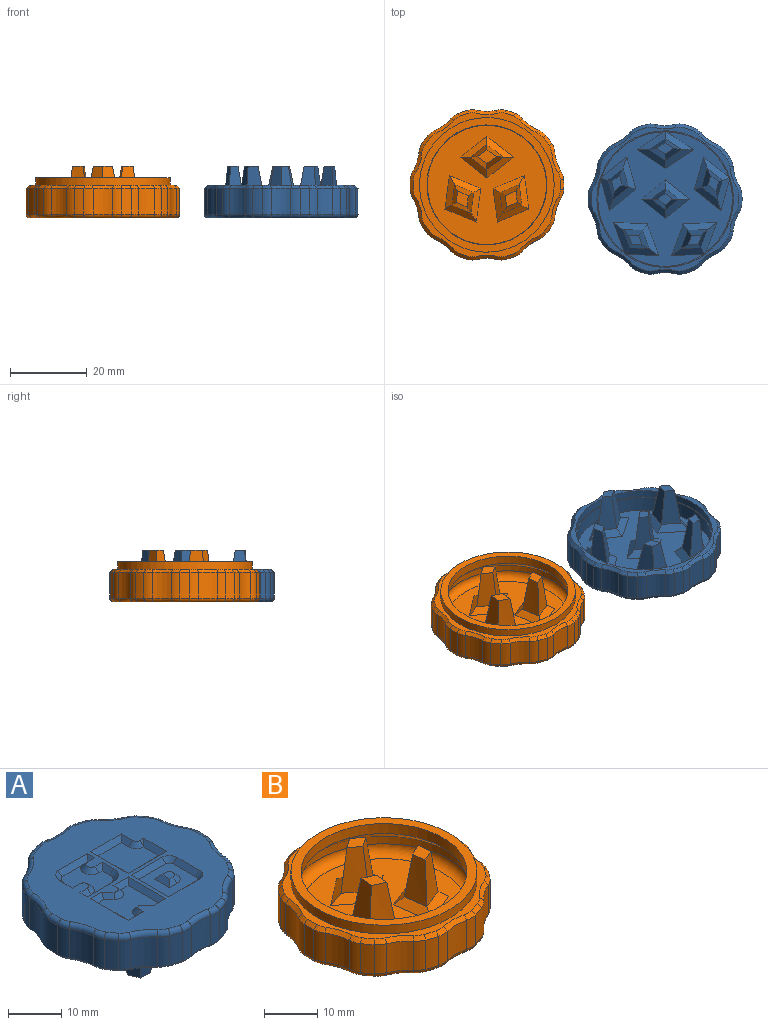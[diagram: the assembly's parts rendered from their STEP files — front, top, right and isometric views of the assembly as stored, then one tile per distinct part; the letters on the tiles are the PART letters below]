
ASSEMBLY  parts=2 mates=1
PART A: 228 faces, bbox 40.8x39.9x13.5 mm
  f0: plane 38x37.08mm, normal (0,0,1), area 717.1mm2, adj f59,f60,f61,f62,f63,f64,f65,f66
  f1: cylinder r=17.5mm len=35mm, axis (0,0,1), area 439.6mm2, adj f2,f33,f35,f37,f39,f45,f47,f49
  f2: plane 35x35mm, normal (0,0,-1), area 545.3mm2, adj f1,f33,f34,f35,f36,f37,f38,f39
  f3: plane 3.55x2.58mm, normal (0,0,-1), area 6.3mm2, adj f4,f5,f6,f7
  f4: bspline ~9.52x5.14mm, area 36.8mm2, adj f3,f5,f7,f53,f55
  f5: bspline ~11x5.19mm, area 36.8mm2, adj f3,f4,f6,f54,f56
  f6: bspline ~11x5.4mm, area 36mm2, adj f3,f5,f7,f56
  f7: bspline ~11x5.07mm, area 36mm2, adj f3,f4,f6,f55
  f8: plane 3.55x2.58mm, normal (0,0,-1), area 6.3mm2, adj f9,f10,f11,f12
  f9: bspline ~11x5.19mm, area 36.8mm2, adj f8,f10,f12,f49,f50
  f10: bspline ~9.52x5.14mm, area 36.8mm2, adj f8,f9,f11,f51,f52
  f11: bspline ~11x5.07mm, area 36mm2, adj f8,f10,f12,f51
  f12: bspline ~11x5.4mm, area 36mm2, adj f8,f9,f11,f49
  f13: plane 4.17x2.73mm, normal (0,0,-1), area 6.3mm2, adj f14,f15,f16,f17
  f14: bspline ~11x4.34mm, area 36.8mm2, adj f13,f15,f17,f45,f46
  f15: bspline ~9.52x4.95mm, area 36.8mm2, adj f13,f14,f16,f47,f48
  f16: bspline ~11x4.24mm, area 36mm2, adj f13,f15,f17,f47
  f17: bspline ~11x5.21mm, area 36mm2, adj f13,f14,f16,f45
  f18: plane 3.8x3.04mm, normal (0,0,-1), area 5.8mm2, adj f19,f20,f21,f22
  f19: plane 9.44x3.49mm, normal (0.62,0.78,-0.1), area 32.7mm2, adj f18,f20,f22,f41
  f20: plane 9.44x3.49mm, normal (0.62,-0.78,-0.1), area 32.7mm2, adj f18,f19,f21,f42
  f21: plane 9.44x3.49mm, normal (-0.62,-0.78,-0.1), area 32.7mm2, adj f18,f20,f22,f44
  f22: plane 9.44x3.49mm, normal (-0.62,0.78,-0.1), area 32.7mm2, adj f18,f19,f21,f43
  f23: plane 4.17x2.73mm, normal (0,0,-1), area 6.3mm2, adj f24,f25,f26,f27
  f24: bspline ~11x5.32mm, area 36.8mm2, adj f23,f25,f27,f33,f34
  f25: bspline ~11x4.34mm, area 36.8mm2, adj f23,f24,f26,f35,f36
  f26: bspline ~11x5.21mm, area 36mm2, adj f23,f25,f27,f35
  f27: bspline ~11x4.24mm, area 36mm2, adj f23,f24,f26,f33
  f28: plane 4.39x2.87mm, normal (0,0,-1), area 6.3mm2, adj f29,f30,f31,f32
  f29: bspline ~11x4.5mm, area 36mm2, adj f28,f30,f32,f37
  f30: bspline ~9.52x4.28mm, area 36.8mm2, adj f28,f29,f31,f37,f38
  f31: bspline ~11x4.6mm, area 36.8mm2, adj f28,f30,f32,f39,f40
  f32: bspline ~11x4.5mm, area 36mm2, adj f28,f29,f31,f39
  f33: bspline ~8.64x7.34mm, area 16mm2, adj f1,f2,f24,f27,f34,f35
  f34: bspline ~8.91x4.02mm, area 15.8mm2, adj f2,f24,f33,f36
  f35: bspline ~9.75x4.27mm, area 16mm2, adj f1,f2,f25,f26,f33,f36
  f36: bspline ~7.94x6.79mm, area 15.8mm2, adj f2,f25,f34,f35
  f37: bspline ~8.99x6.79mm, area 16mm2, adj f1,f2,f29,f30,f38,f39
  f38: bspline ~8.25x6.29mm, area 15.8mm2, adj f2,f30,f37,f40
  f39: bspline ~8.99x6.79mm, area 16mm2, adj f1,f2,f31,f32,f37,f40
  f40: bspline ~8.25x6.29mm, area 15.8mm2, adj f2,f31,f38,f39
  f41: plane 6.26x5.01mm, normal (0.42,0.52,-0.74), area 14.5mm2, adj f2,f19,f42,f43
  f42: plane 6.26x5.01mm, normal (0.42,-0.52,-0.74), area 14.5mm2, adj f2,f20,f41,f44
  f43: plane 6.26x5.01mm, normal (-0.42,0.52,-0.74), area 14.5mm2, adj f2,f22,f41,f44
  f44: plane 6.26x5.01mm, normal (-0.42,-0.52,-0.74), area 14.5mm2, adj f2,f21,f42,f43
  f45: bspline ~9.75x4.27mm, area 16mm2, adj f1,f2,f14,f17,f46,f47
  f46: bspline ~7.94x6.79mm, area 15.8mm2, adj f2,f14,f45,f48
  f47: bspline ~8.64x7.34mm, area 16mm2, adj f1,f2,f15,f16,f45,f48
  f48: bspline ~8.91x4.02mm, area 15.8mm2, adj f2,f15,f46,f47
  f49: bspline ~8.71x2.09mm, area 16mm2, adj f1,f2,f9,f12,f50,f51
  f50: bspline ~8.82x4.66mm, area 15.8mm2, adj f2,f9,f49,f52
  f51: bspline ~9.64x4.98mm, area 16mm2, adj f1,f2,f10,f11,f49,f52
  f52: bspline ~9.71x2.11mm, area 15.8mm2, adj f2,f10,f50,f51
  f53: bspline ~9.71x2.11mm, area 15.8mm2, adj f2,f4,f54,f55
  f54: bspline ~8.82x4.66mm, area 15.8mm2, adj f2,f5,f53,f56
  f55: bspline ~9.64x4.98mm, area 16mm2, adj f1,f2,f4,f7,f53,f56
  f56: bspline ~8.71x2.09mm, area 16mm2, adj f1,f2,f5,f6,f54,f55
  f57: cylinder r=17.75mm len=35.5mm, axis (0,0,-1), area 223.1mm2, adj f58,f139
  f58: plane 35.5x35.5mm, normal (0,0,-1), area 27.7mm2, adj f1,f57
  f59: torus R=4mm, axis (0,0,1), area 3.5mm2, adj f0,f60,f98,f99
  f60: torus R=11.9mm, axis (0,0,1), area 8.3mm2, adj f0,f59,f61,f100
  f61: torus R=4mm, axis (0,0,1), area 3.5mm2, adj f0,f60,f62,f101
  f62: torus R=19mm, axis (0,0,1), area 4mm2, adj f0,f61,f63,f102
  f63: torus R=4mm, axis (0,0,1), area 3.5mm2, adj f0,f62,f64,f103
  f64: torus R=11.9mm, axis (0,0,1), area 8.3mm2, adj f0,f63,f65,f104
  f65: torus R=4mm, axis (0,0,1), area 3.5mm2, adj f0,f64,f66,f105
  f66: torus R=19mm, axis (0,0,1), area 4mm2, adj f0,f65,f67,f106
  f67: torus R=4mm, axis (0,0,1), area 3.5mm2, adj f0,f66,f68,f107
  f68: torus R=11.9mm, axis (0,0,1), area 8.3mm2, adj f0,f67,f69,f108
  f69: torus R=4mm, axis (0,0,1), area 3.5mm2, adj f0,f68,f70,f109
  f70: torus R=19mm, axis (0,0,1), area 4mm2, adj f0,f69,f71,f110
  f71: torus R=4mm, axis (0,0,1), area 3.5mm2, adj f0,f70,f72,f111
  f72: torus R=11.9mm, axis (0,0,1), area 8.3mm2, adj f0,f71,f73,f112
  f73: torus R=4mm, axis (0,0,1), area 3.5mm2, adj f0,f72,f74,f113
  f74: torus R=19mm, axis (0,0,1), area 4mm2, adj f0,f73,f75,f114
  f75: torus R=4mm, axis (0,0,1), area 3.5mm2, adj f0,f74,f76,f115
  f76: torus R=11.9mm, axis (0,0,1), area 8.3mm2, adj f0,f75,f77,f116
  f77: torus R=4mm, axis (0,0,1), area 3.5mm2, adj f0,f76,f78,f117
  f78: torus R=19mm, axis (0,0,1), area 4mm2, adj f0,f77,f79,f118
  f79: torus R=4mm, axis (0,0,1), area 3.5mm2, adj f0,f78,f80,f119
  f80: torus R=11.9mm, axis (0,0,1), area 8.3mm2, adj f0,f79,f81,f120
  f81: torus R=4mm, axis (0,0,1), area 3.5mm2, adj f0,f80,f82,f121
  f82: torus R=19mm, axis (0,0,1), area 4mm2, adj f0,f81,f83,f122
  f83: torus R=4mm, axis (0,0,1), area 3.5mm2, adj f0,f82,f84,f123
  f84: torus R=11.9mm, axis (0,0,1), area 8.3mm2, adj f0,f83,f85,f124
  f85: torus R=4mm, axis (0,0,1), area 3.5mm2, adj f0,f84,f86,f125
  f86: torus R=19mm, axis (0,0,1), area 4mm2, adj f0,f85,f87,f126
  f87: torus R=4mm, axis (0,0,1), area 3.5mm2, adj f0,f86,f88,f127
  f88: torus R=11.9mm, axis (0,0,1), area 8.3mm2, adj f0,f87,f89,f128
  f89: torus R=4mm, axis (0,0,1), area 3.5mm2, adj f0,f88,f90,f129
  f90: torus R=19mm, axis (0,0,1), area 4mm2, adj f0,f89,f91,f130
  f91: torus R=4mm, axis (0,0,1), area 3.5mm2, adj f0,f90,f92,f131
  f92: torus R=11.9mm, axis (0,0,1), area 8.3mm2, adj f0,f91,f93,f132
  f93: torus R=4mm, axis (0,0,1), area 3.5mm2, adj f0,f92,f94,f133
  f94: torus R=19mm, axis (0,0,1), area 4mm2, adj f0,f93,f95,f134
  f95: torus R=4mm, axis (0,0,1), area 3.5mm2, adj f0,f94,f96,f135
  f96: torus R=11.9mm, axis (0,0,1), area 8.3mm2, adj f0,f95,f97,f136
  f97: torus R=4mm, axis (0,0,1), area 3.5mm2, adj f0,f96,f98,f137
  f98: torus R=19mm, axis (0,0,1), area 4mm2, adj f0,f59,f97,f138
  f99: cylinder r=5mm len=6.7mm, axis (0,0,1), area 16.2mm2, adj f59,f100,f138,f208
  f100: cylinder r=10.9mm len=6.7mm, axis (0,0,-1), area 34.2mm2, adj f60,f99,f101,f210
  f101: cylinder r=5mm len=6.7mm, axis (0,0,1), area 16.2mm2, adj f61,f100,f102,f212
  f102: cylinder r=20mm len=6.7mm, axis (0,0,-1), area 17.6mm2, adj f62,f101,f103,f214
  f103: cylinder r=5mm len=6.7mm, axis (0,0,1), area 16.2mm2, adj f63,f102,f104,f216
  f104: cylinder r=10.9mm len=6.7mm, axis (0,0,-1), area 34.2mm2, adj f64,f103,f105,f218
  f105: cylinder r=5mm len=6.7mm, axis (0,0,1), area 16.2mm2, adj f65,f104,f106,f220
  f106: cylinder r=20mm len=6.7mm, axis (0,0,-1), area 17.6mm2, adj f66,f105,f107,f222
  f107: cylinder r=5mm len=6.7mm, axis (0,0,1), area 16.2mm2, adj f67,f106,f108,f224
  f108: cylinder r=10.9mm len=6.7mm, axis (0,0,-1), area 34.2mm2, adj f68,f107,f109,f226
  f109: cylinder r=5mm len=6.7mm, axis (0,0,1), area 16.2mm2, adj f69,f108,f110,f227
  f110: cylinder r=20mm len=6.7mm, axis (0,0,-1), area 17.6mm2, adj f70,f109,f111,f225
  f111: cylinder r=5mm len=6.7mm, axis (0,0,1), area 16.2mm2, adj f71,f110,f112,f223
  f112: cylinder r=10.9mm len=6.7mm, axis (0,0,-1), area 34.2mm2, adj f72,f111,f113,f221
  f113: cylinder r=5mm len=6.7mm, axis (0,0,1), area 16.2mm2, adj f73,f112,f114,f219
  f114: cylinder r=20mm len=6.7mm, axis (0,0,-1), area 17.6mm2, adj f74,f113,f115,f217
  f115: cylinder r=5mm len=6.7mm, axis (0,0,1), area 16.2mm2, adj f75,f114,f116,f215
  f116: cylinder r=10.9mm len=6.7mm, axis (0,0,-1), area 34.2mm2, adj f76,f115,f117,f213
  f117: cylinder r=5mm len=6.7mm, axis (0,0,1), area 16.2mm2, adj f77,f116,f118,f211
  f118: cylinder r=20mm len=6.7mm, axis (0,0,-1), area 17.6mm2, adj f78,f117,f119,f209
  f119: cylinder r=5mm len=6.7mm, axis (0,0,1), area 16.2mm2, adj f79,f118,f120,f207
  f120: cylinder r=10.9mm len=6.7mm, axis (0,0,-1), area 34.2mm2, adj f80,f119,f121,f205
  f121: cylinder r=5mm len=6.7mm, axis (0,0,1), area 16.2mm2, adj f81,f120,f122,f203
  f122: cylinder r=20mm len=6.7mm, axis (0,0,-1), area 17.6mm2, adj f82,f121,f123,f201
  f123: cylinder r=5mm len=6.7mm, axis (0,0,1), area 16.2mm2, adj f83,f122,f124,f199
  f124: cylinder r=10.9mm len=6.7mm, axis (0,0,-1), area 34.2mm2, adj f84,f123,f125,f197
  f125: cylinder r=5mm len=6.7mm, axis (0,0,1), area 16.2mm2, adj f85,f124,f126,f195
  f126: cylinder r=20mm len=6.7mm, axis (0,0,-1), area 17.6mm2, adj f86,f125,f127,f193
  f127: cylinder r=5mm len=6.7mm, axis (0,0,1), area 16.2mm2, adj f87,f126,f128,f191
  f128: cylinder r=10.9mm len=6.7mm, axis (0,0,-1), area 34.2mm2, adj f88,f127,f129,f189
  f129: cylinder r=5mm len=6.7mm, axis (0,0,1), area 16.2mm2, adj f89,f128,f130,f188
  f130: cylinder r=20mm len=6.7mm, axis (0,0,-1), area 17.6mm2, adj f90,f129,f131,f190
  f131: cylinder r=5mm len=6.7mm, axis (0,0,1), area 16.2mm2, adj f91,f130,f132,f192
  f132: cylinder r=10.9mm len=6.7mm, axis (0,0,-1), area 34.2mm2, adj f92,f131,f133,f194
  f133: cylinder r=5mm len=6.7mm, axis (0,0,1), area 16.2mm2, adj f93,f132,f134,f196
  f134: cylinder r=20mm len=6.7mm, axis (0,0,-1), area 17.6mm2, adj f94,f133,f135,f198
  f135: cylinder r=5mm len=6.7mm, axis (0,0,1), area 16.2mm2, adj f95,f134,f136,f200
  f136: cylinder r=10.9mm len=6.7mm, axis (0,0,-1), area 34.2mm2, adj f96,f135,f137,f202
  f137: cylinder r=5mm len=6.7mm, axis (0,0,1), area 16.2mm2, adj f97,f136,f138,f204
  f138: cylinder r=20mm len=6.7mm, axis (0,0,-1), area 17.6mm2, adj f98,f99,f137,f206
  f139: plane 38.4x37.48mm, normal (0,0,-1), area 123.8mm2, adj f57,f188,f189,f190,f191,f192,f193,f194
  f140: plane 3x1mm, normal (0,0.71,0.71), area 3.2mm2, adj f0,f141,f151,f152
  f141: plane 10x1mm, normal (-0.71,0,0.71), area 12.7mm2, adj f0,f140,f142,f152
  f142: plane 4x1mm, normal (0,-0.71,0.71), area 4.2mm2, adj f0,f141,f143,f152
  f143: plane 1.07x1mm, normal (0.71,0,0.71), area 0.8mm2, adj f0,f142,f144,f152
  f144: cone r=0.8mm half-angle=45deg, axis (0,0,-1), area 4.3mm2, adj f0,f143,f145,f152
  f145: plane 2.34x2.05mm, normal (-0.5,-0.5,0.71), area 3mm2, adj f0,f144,f146,f152
  f146: plane 3x1mm, normal (0,-0.71,0.71), area 3.2mm2, adj f0,f145,f147,f152
  f147: plane 10x1mm, normal (0.71,0,0.71), area 12.7mm2, adj f0,f146,f148,f152
  f148: plane 4x1mm, normal (0,0.71,0.71), area 4.2mm2, adj f0,f147,f149,f152
  f149: plane 1.07x1mm, normal (-0.71,0,0.71), area 0.8mm2, adj f0,f148,f150,f152
  f150: cone r=0.8mm half-angle=45deg, axis (0,0,-1), area 4.3mm2, adj f0,f149,f151,f152
  f151: plane 2.34x2.05mm, normal (0.5,0.5,0.71), area 3mm2, adj f0,f140,f150,f152
  f152: plane 8x8mm, normal (0,0,1), area 52.5mm2, adj f140,f141,f142,f143,f144,f145,f146,f147
  f153: plane 10.2x1mm, normal (0,0.71,0.71), area 13mm2, adj f0,f154,f159,f160
  f154: plane 6x1mm, normal (-0.71,0,0.71), area 7.1mm2, adj f0,f153,f155,f160
  f155: plane 1x1mm, normal (0,-0.71,0.71), area 0.7mm2, adj f0,f154,f156
  f156: cone r=1mm half-angle=45deg, axis (0,0,-1), area 3.3mm2, adj f0,f155,f157,f160
  f157: plane 3x1mm, normal (-0.71,0,0.71), area 3.5mm2, adj f0,f156,f158,f160
  f158: plane 8.2x1mm, normal (0,-0.71,0.71), area 10.2mm2, adj f0,f157,f159,f160
  f159: plane 10x1mm, normal (0.71,0,0.71), area 12.7mm2, adj f0,f153,f158,f160
  f160: plane 8.2x8mm, normal (0,0,1), area 58.5mm2, adj f153,f154,f156,f157,f158,f159
  f161: cone r=3mm half-angle=45deg, axis (0,0,1), area 4.2mm2, adj f0,f162,f174,f175
  f162: plane 3.17x1mm, normal (0.71,0,0.71), area 3.8mm2, adj f0,f161,f163,f175
  f163: plane 2x1mm, normal (0,0.71,0.71), area 2.1mm2, adj f0,f162,f164,f175
  f164: cone r=1mm half-angle=45deg, axis (0,0,-1), area 6.7mm2, adj f0,f163,f165,f175
  f165: plane 2x1mm, normal (0,-0.71,0.71), area 2.1mm2, adj f0,f164,f166,f167
  f166: plane 2x1mm, normal (0.71,0,0.71), area 1.4mm2, adj f0,f165,f167
  f167: plane 7x1mm, normal (0,0.71,0.71), area 9.2mm2, adj f0,f165,f166,f168,f175
  f168: cone r=3mm half-angle=45deg, axis (0,0,1), area 5.6mm2, adj f0,f167,f169,f175
  f169: plane 3x1mm, normal (-0.71,0,0.71), area 3.5mm2, adj f0,f168,f170,f175
  f170: plane 2x1mm, normal (0,-0.71,0.71), area 2.1mm2, adj f0,f169,f171,f175
  f171: cone r=1mm half-angle=45deg, axis (0,0,-1), area 6.7mm2, adj f0,f170,f172,f175
  f172: plane 2x1mm, normal (0,0.71,0.71), area 2.1mm2, adj f0,f171,f173,f174
  f173: plane 2x1mm, normal (-0.71,0,0.71), area 1.4mm2, adj f0,f172,f174
  f174: plane 8.03x1.03mm, normal (0,-0.71,0.71), area 10.5mm2, adj f0,f161,f172,f173,f175
  f175: plane 8x8mm, normal (0,0,1), area 42mm2, adj f161,f162,f163,f164,f167,f168,f169,f170
  f176: plane 6x1mm, normal (-0.71,0,0.71), area 8.5mm2, adj f0,f177,f185,f186
  f177: cone r=2mm half-angle=45deg, axis (0,0,1), area 3.3mm2, adj f0,f176,f178,f186
  f178: plane 8.2x1mm, normal (0,-0.71,0.71), area 10.9mm2, adj f0,f177,f179,f186
  f179: plane 10x1mm, normal (0.71,0,0.71), area 12.7mm2, adj f0,f178,f180,f186
  f180: plane 8.2x1mm, normal (0,0.71,0.71), area 10.9mm2, adj f0,f179,f185,f186
  f181: cone r=1mm half-angle=45deg, axis (0,0,-1), area 6.7mm2, adj f182,f184,f186,f187
  f182: plane 2x1mm, normal (0,-0.71,0.71), area 2.1mm2, adj f181,f183,f186,f187
  f183: plane 4x1mm, normal (-0.71,0,0.71), area 4.2mm2, adj f182,f184,f186,f187
  f184: plane 2x1mm, normal (0,0.71,0.71), area 2.1mm2, adj f181,f183,f186,f187
  f185: cone r=2mm half-angle=45deg, axis (0,0,1), area 3.3mm2, adj f0,f176,f180,f186
  f186: plane 8.2x8mm, normal (0,0,1), area 50.9mm2, adj f176,f177,f178,f179,f180,f181,f182,f183
  f187: plane 2x2mm, normal (0,0,1), area 3.6mm2, adj f181,f182,f183,f184
  f188: cone r=4.2mm half-angle=45deg, axis (0,0,1), area 2.5mm2, adj f129,f139,f189,f190
  f189: cone r=11.7mm half-angle=45deg, axis (0,0,-1), area 6mm2, adj f128,f139,f188,f191
  f190: cone r=20mm half-angle=45deg, axis (0,0,1), area 2.9mm2, adj f130,f139,f188,f192
  f191: cone r=4.2mm half-angle=45deg, axis (0,0,1), area 2.5mm2, adj f127,f139,f189,f193
  f192: cone r=4.2mm half-angle=45deg, axis (0,0,1), area 2.5mm2, adj f131,f139,f190,f194
  f193: cone r=20mm half-angle=45deg, axis (0,0,1), area 2.9mm2, adj f126,f139,f191,f195
  f194: cone r=11.7mm half-angle=45deg, axis (0,0,-1), area 6mm2, adj f132,f139,f192,f196
  f195: cone r=4.2mm half-angle=45deg, axis (0,0,1), area 2.5mm2, adj f125,f139,f193,f197
  f196: cone r=4.2mm half-angle=45deg, axis (0,0,1), area 2.5mm2, adj f133,f139,f194,f198
  f197: cone r=11.7mm half-angle=45deg, axis (0,0,-1), area 6mm2, adj f124,f139,f195,f199
  f198: cone r=20mm half-angle=45deg, axis (0,0,1), area 2.9mm2, adj f134,f139,f196,f200
  f199: cone r=4.2mm half-angle=45deg, axis (0,0,1), area 2.5mm2, adj f123,f139,f197,f201
  f200: cone r=4.2mm half-angle=45deg, axis (0,0,1), area 2.5mm2, adj f135,f139,f198,f202
  f201: cone r=20mm half-angle=45deg, axis (0,0,1), area 2.9mm2, adj f122,f139,f199,f203
  f202: cone r=11.7mm half-angle=45deg, axis (0,0,-1), area 6mm2, adj f136,f139,f200,f204
  f203: cone r=4.2mm half-angle=45deg, axis (0,0,1), area 2.5mm2, adj f121,f139,f201,f205
  f204: cone r=4.2mm half-angle=45deg, axis (0,0,1), area 2.5mm2, adj f137,f139,f202,f206
  f205: cone r=11.7mm half-angle=45deg, axis (0,0,-1), area 6mm2, adj f120,f139,f203,f207
  f206: cone r=20mm half-angle=45deg, axis (0,0,1), area 2.9mm2, adj f138,f139,f204,f208
  f207: cone r=4.2mm half-angle=45deg, axis (0,0,1), area 2.5mm2, adj f119,f139,f205,f209
  f208: cone r=4.2mm half-angle=45deg, axis (0,0,1), area 2.5mm2, adj f99,f139,f206,f210
  f209: cone r=20mm half-angle=45deg, axis (0,0,1), area 2.9mm2, adj f118,f139,f207,f211
  f210: cone r=11.7mm half-angle=45deg, axis (0,0,-1), area 6mm2, adj f100,f139,f208,f212
  f211: cone r=4.2mm half-angle=45deg, axis (0,0,1), area 2.5mm2, adj f117,f139,f209,f213
  f212: cone r=4.2mm half-angle=45deg, axis (0,0,1), area 2.5mm2, adj f101,f139,f210,f214
  f213: cone r=11.7mm half-angle=45deg, axis (0,0,-1), area 6mm2, adj f116,f139,f211,f215
  f214: cone r=20mm half-angle=45deg, axis (0,0,1), area 2.9mm2, adj f102,f139,f212,f216
  f215: cone r=4.2mm half-angle=45deg, axis (0,0,1), area 2.5mm2, adj f115,f139,f213,f217
  f216: cone r=4.2mm half-angle=45deg, axis (0,0,1), area 2.5mm2, adj f103,f139,f214,f218
  f217: cone r=20mm half-angle=45deg, axis (0,0,1), area 2.9mm2, adj f114,f139,f215,f219
  f218: cone r=11.7mm half-angle=45deg, axis (0,0,-1), area 6mm2, adj f104,f139,f216,f220
  f219: cone r=4.2mm half-angle=45deg, axis (0,0,1), area 2.5mm2, adj f113,f139,f217,f221
  f220: cone r=4.2mm half-angle=45deg, axis (0,0,1), area 2.5mm2, adj f105,f139,f218,f222
  f221: cone r=11.7mm half-angle=45deg, axis (0,0,-1), area 6mm2, adj f112,f139,f219,f223
  f222: cone r=20mm half-angle=45deg, axis (0,0,1), area 2.9mm2, adj f106,f139,f220,f224
  f223: cone r=4.2mm half-angle=45deg, axis (0,0,1), area 2.5mm2, adj f111,f139,f221,f225
  f224: cone r=4.2mm half-angle=45deg, axis (0,0,1), area 2.5mm2, adj f107,f139,f222,f226
  f225: cone r=20mm half-angle=45deg, axis (0,0,1), area 2.9mm2, adj f110,f139,f223,f227
  f226: cone r=11.7mm half-angle=45deg, axis (0,0,-1), area 6mm2, adj f108,f139,f224,f227
  f227: cone r=4.2mm half-angle=45deg, axis (0,0,1), area 2.5mm2, adj f109,f139,f225,f226
PART B: 156 faces, bbox 40.7x39.9x13.5 mm
  f0: cylinder r=17.5mm len=35mm, axis (0,0,-1), area 197.9mm2, adj f30,f55
  f1: plane 31x31mm, normal (0,0,1), area 530.3mm2, adj f17,f18,f19,f20,f21,f22,f23,f24
  f2: plane 4.36x3.05mm, normal (0,0,1), area 8.9mm2, adj f3,f4,f5,f6
  f3: bspline ~11x5.28mm, area 40.4mm2, adj f2,f4,f6,f17
  f4: bspline ~9.51x5.3mm, area 40.2mm2, adj f2,f3,f5,f18
  f5: bspline ~9.51x4.94mm, area 40.3mm2, adj f2,f4,f6,f20
  f6: bspline ~11x5.65mm, area 40.5mm2, adj f2,f3,f5,f19
  f7: plane 5.03x3.52mm, normal (0,0,1), area 8.9mm2, adj f8,f9,f10,f11
  f8: bspline ~11x4.5mm, area 40.3mm2, adj f7,f9,f11,f22
  f9: bspline ~11x4.5mm, area 40.5mm2, adj f7,f8,f10,f24
  f10: bspline ~11x4.5mm, area 40.4mm2, adj f7,f9,f11,f23
  f11: bspline ~11x4.5mm, area 40.2mm2, adj f7,f8,f10,f21
  f12: plane 4.36x3.05mm, normal (0,0,1), area 8.9mm2, adj f13,f14,f15,f16
  f13: bspline ~11x5.65mm, area 40.4mm2, adj f12,f14,f16,f26
  f14: bspline ~11x5.28mm, area 40.2mm2, adj f12,f13,f15,f28
  f15: bspline ~9.51x5.3mm, area 40.3mm2, adj f12,f14,f16,f27
  f16: bspline ~11x5.28mm, area 40.5mm2, adj f12,f13,f15,f25
  f17: bspline ~8.77x4.88mm, area 15.6mm2, adj f1,f3,f18,f19
  f18: bspline ~9.81x2.95mm, area 15.8mm2, adj f1,f4,f17,f20
  f19: bspline ~8.94x2.83mm, area 15.6mm2, adj f1,f6,f17,f20
  f20: bspline ~9.58x5.22mm, area 15.8mm2, adj f1,f5,f18,f19
  f21: bspline ~8.68x7.23mm, area 15.8mm2, adj f1,f11,f22,f23
  f22: bspline ~8.68x7.23mm, area 15.8mm2, adj f1,f8,f21,f24
  f23: bspline ~8.68x7.23mm, area 15.6mm2, adj f1,f10,f21,f24
  f24: bspline ~8.68x7.23mm, area 15.6mm2, adj f1,f9,f22,f23
  f25: bspline ~8.77x4.88mm, area 15.6mm2, adj f1,f16,f26,f27
  f26: bspline ~8.94x2.83mm, area 15.6mm2, adj f1,f13,f25,f28
  f27: bspline ~9.81x2.95mm, area 15.8mm2, adj f1,f15,f25,f28
  f28: bspline ~9.58x5.22mm, area 15.8mm2, adj f1,f14,f26,f27
  f29: cylinder r=15.6mm len=31.2mm, axis (0,0,1), area 225.4mm2, adj f30,f32
  f30: cone r=17.5mm half-angle=45deg, axis (0,0,-1), area 279.4mm2, adj f0,f29
  f31: cylinder r=17.5mm len=35mm, axis (0,0,-1), area 219.9mm2, adj f32,f54
  f32: plane 35x35mm, normal (0,0,1), area 197.6mm2, adj f29,f31
  f33: plane 38x37.08mm, normal (0,0,-1), area 1089.6mm2, adj f76,f77,f78,f79,f80,f81,f82,f83
  f34: cylinder r=20mm len=6.7mm, axis (0,0,-1), area 17.6mm2, adj f74,f75,f110,f145
  f35: cylinder r=10.9mm len=6.7mm, axis (0,0,-1), area 34.2mm2, adj f73,f74,f106,f141
  f36: cylinder r=20mm len=6.7mm, axis (0,0,-1), area 17.6mm2, adj f72,f73,f102,f137
  f37: cylinder r=10.9mm len=6.7mm, axis (0,0,-1), area 34.2mm2, adj f71,f72,f98,f133
  f38: cylinder r=20mm len=6.7mm, axis (0,0,-1), area 17.6mm2, adj f70,f71,f94,f129
  f39: cylinder r=10.9mm len=6.7mm, axis (0,0,-1), area 34.2mm2, adj f69,f70,f90,f125
  f40: cylinder r=20mm len=6.7mm, axis (0,0,-1), area 17.6mm2, adj f68,f69,f86,f121
  f41: cylinder r=10.9mm len=6.7mm, axis (0,0,-1), area 34.2mm2, adj f67,f68,f82,f117
  f42: cylinder r=20mm len=6.7mm, axis (0,0,-1), area 17.6mm2, adj f66,f67,f78,f118
  f43: cylinder r=10.9mm len=6.7mm, axis (0,0,-1), area 34.2mm2, adj f65,f66,f77,f122
  f44: cylinder r=20mm len=6.7mm, axis (0,0,-1), area 17.6mm2, adj f64,f65,f81,f126
  f45: cylinder r=10.9mm len=6.7mm, axis (0,0,-1), area 34.2mm2, adj f63,f64,f85,f130
  f46: cylinder r=20mm len=6.7mm, axis (0,0,-1), area 17.6mm2, adj f62,f63,f89,f134
  f47: cylinder r=10.9mm len=6.7mm, axis (0,0,-1), area 34.2mm2, adj f61,f62,f93,f138
  f48: cylinder r=20mm len=6.7mm, axis (0,0,-1), area 17.6mm2, adj f60,f61,f97,f142
  f49: cylinder r=10.9mm len=6.7mm, axis (0,0,-1), area 34.2mm2, adj f59,f60,f101,f146
  f50: cylinder r=20mm len=6.7mm, axis (0,0,-1), area 17.6mm2, adj f58,f59,f105,f150
  f51: cylinder r=10.9mm len=6.7mm, axis (0,0,-1), area 34.2mm2, adj f57,f58,f109,f154
  f52: cylinder r=20mm len=6.7mm, axis (0,0,-1), area 17.6mm2, adj f56,f57,f113,f153
  f53: cylinder r=10.9mm len=6.7mm, axis (0,0,-1), area 34.2mm2, adj f56,f75,f114,f149
  f54: plane 38.4x37.48mm, normal (0,0,1), area 151.5mm2, adj f31,f116,f117,f118,f119,f120,f121,f122
  f55: torus R=15.5mm, axis (0,0,1), area 331.1mm2, adj f0,f1
  f56: cylinder r=5mm len=6.7mm, axis (0,0,1), area 16.2mm2, adj f52,f53,f115,f151
  f57: cylinder r=5mm len=6.7mm, axis (0,0,1), area 16.2mm2, adj f51,f52,f111,f155
  f58: cylinder r=5mm len=6.7mm, axis (0,0,1), area 16.2mm2, adj f50,f51,f107,f152
  f59: cylinder r=5mm len=6.7mm, axis (0,0,1), area 16.2mm2, adj f49,f50,f103,f148
  f60: cylinder r=5mm len=6.7mm, axis (0,0,1), area 16.2mm2, adj f48,f49,f99,f144
  f61: cylinder r=5mm len=6.7mm, axis (0,0,1), area 16.2mm2, adj f47,f48,f95,f140
  f62: cylinder r=5mm len=6.7mm, axis (0,0,1), area 16.2mm2, adj f46,f47,f91,f136
  f63: cylinder r=5mm len=6.7mm, axis (0,0,1), area 16.2mm2, adj f45,f46,f87,f132
  f64: cylinder r=5mm len=6.7mm, axis (0,0,1), area 16.2mm2, adj f44,f45,f83,f128
  f65: cylinder r=5mm len=6.7mm, axis (0,0,1), area 16.2mm2, adj f43,f44,f79,f124
  f66: cylinder r=5mm len=6.7mm, axis (0,0,1), area 16.2mm2, adj f42,f43,f76,f120
  f67: cylinder r=5mm len=6.7mm, axis (0,0,1), area 16.2mm2, adj f41,f42,f80,f116
  f68: cylinder r=5mm len=6.7mm, axis (0,0,1), area 16.2mm2, adj f40,f41,f84,f119
  f69: cylinder r=5mm len=6.7mm, axis (0,0,1), area 16.2mm2, adj f39,f40,f88,f123
  f70: cylinder r=5mm len=6.7mm, axis (0,0,1), area 16.2mm2, adj f38,f39,f92,f127
  f71: cylinder r=5mm len=6.7mm, axis (0,0,1), area 16.2mm2, adj f37,f38,f96,f131
  f72: cylinder r=5mm len=6.7mm, axis (0,0,1), area 16.2mm2, adj f36,f37,f100,f135
  f73: cylinder r=5mm len=6.7mm, axis (0,0,1), area 16.2mm2, adj f35,f36,f104,f139
  f74: cylinder r=5mm len=6.7mm, axis (0,0,1), area 16.2mm2, adj f34,f35,f108,f143
  f75: cylinder r=5mm len=6.7mm, axis (0,0,1), area 16.2mm2, adj f34,f53,f112,f147
  f76: torus R=4mm, axis (0,0,1), area 3.5mm2, adj f33,f66,f77,f78
  f77: torus R=11.9mm, axis (0,0,1), area 8.3mm2, adj f33,f43,f76,f79
  f78: torus R=19mm, axis (0,0,1), area 4mm2, adj f33,f42,f76,f80
  f79: torus R=4mm, axis (0,0,1), area 3.5mm2, adj f33,f65,f77,f81
  f80: torus R=4mm, axis (0,0,1), area 3.5mm2, adj f33,f67,f78,f82
  f81: torus R=19mm, axis (0,0,1), area 4mm2, adj f33,f44,f79,f83
  f82: torus R=11.9mm, axis (0,0,1), area 8.3mm2, adj f33,f41,f80,f84
  f83: torus R=4mm, axis (0,0,1), area 3.5mm2, adj f33,f64,f81,f85
  f84: torus R=4mm, axis (0,0,1), area 3.5mm2, adj f33,f68,f82,f86
  f85: torus R=11.9mm, axis (0,0,1), area 8.3mm2, adj f33,f45,f83,f87
  f86: torus R=19mm, axis (0,0,1), area 4mm2, adj f33,f40,f84,f88
  f87: torus R=4mm, axis (0,0,1), area 3.5mm2, adj f33,f63,f85,f89
  f88: torus R=4mm, axis (0,0,1), area 3.5mm2, adj f33,f69,f86,f90
  f89: torus R=19mm, axis (0,0,1), area 4mm2, adj f33,f46,f87,f91
  f90: torus R=11.9mm, axis (0,0,1), area 8.3mm2, adj f33,f39,f88,f92
  f91: torus R=4mm, axis (0,0,1), area 3.5mm2, adj f33,f62,f89,f93
  f92: torus R=4mm, axis (0,0,1), area 3.5mm2, adj f33,f70,f90,f94
  f93: torus R=11.9mm, axis (0,0,1), area 8.3mm2, adj f33,f47,f91,f95
  f94: torus R=19mm, axis (0,0,1), area 4mm2, adj f33,f38,f92,f96
  f95: torus R=4mm, axis (0,0,1), area 3.5mm2, adj f33,f61,f93,f97
  f96: torus R=4mm, axis (0,0,1), area 3.5mm2, adj f33,f71,f94,f98
  f97: torus R=19mm, axis (0,0,1), area 4mm2, adj f33,f48,f95,f99
  f98: torus R=11.9mm, axis (0,0,1), area 8.3mm2, adj f33,f37,f96,f100
  f99: torus R=4mm, axis (0,0,1), area 3.5mm2, adj f33,f60,f97,f101
  f100: torus R=4mm, axis (0,0,1), area 3.5mm2, adj f33,f72,f98,f102
  f101: torus R=11.9mm, axis (0,0,1), area 8.3mm2, adj f33,f49,f99,f103
  f102: torus R=19mm, axis (0,0,1), area 4mm2, adj f33,f36,f100,f104
  f103: torus R=4mm, axis (0,0,1), area 3.5mm2, adj f33,f59,f101,f105
  f104: torus R=4mm, axis (0,0,1), area 3.5mm2, adj f33,f73,f102,f106
  f105: torus R=19mm, axis (0,0,1), area 4mm2, adj f33,f50,f103,f107
  f106: torus R=11.9mm, axis (0,0,1), area 8.3mm2, adj f33,f35,f104,f108
  f107: torus R=4mm, axis (0,0,1), area 3.5mm2, adj f33,f58,f105,f109
  f108: torus R=4mm, axis (0,0,1), area 3.5mm2, adj f33,f74,f106,f110
  f109: torus R=11.9mm, axis (0,0,1), area 8.3mm2, adj f33,f51,f107,f111
  f110: torus R=19mm, axis (0,0,1), area 4mm2, adj f33,f34,f108,f112
  f111: torus R=4mm, axis (0,0,1), area 3.5mm2, adj f33,f57,f109,f113
  f112: torus R=4mm, axis (0,0,1), area 3.5mm2, adj f33,f75,f110,f114
  f113: torus R=19mm, axis (0,0,1), area 4mm2, adj f33,f52,f111,f115
  f114: torus R=11.9mm, axis (0,0,1), area 8.3mm2, adj f33,f53,f112,f115
  f115: torus R=4mm, axis (0,0,1), area 3.5mm2, adj f33,f56,f113,f114
  f116: cone r=4.2mm half-angle=45deg, axis (0,0,-1), area 2.5mm2, adj f54,f67,f117,f118
  f117: cone r=10.9mm half-angle=45deg, axis (0,0,1), area 6mm2, adj f41,f54,f116,f119
  f118: cone r=19.2mm half-angle=45deg, axis (0,0,-1), area 2.9mm2, adj f42,f54,f116,f120
  f119: cone r=4.2mm half-angle=45deg, axis (0,0,-1), area 2.5mm2, adj f54,f68,f117,f121
  f120: cone r=4.2mm half-angle=45deg, axis (0,0,-1), area 2.5mm2, adj f54,f66,f118,f122
  f121: cone r=19.2mm half-angle=45deg, axis (0,0,-1), area 2.9mm2, adj f40,f54,f119,f123
  f122: cone r=10.9mm half-angle=45deg, axis (0,0,1), area 6mm2, adj f43,f54,f120,f124
  f123: cone r=4.2mm half-angle=45deg, axis (0,0,-1), area 2.5mm2, adj f54,f69,f121,f125
  f124: cone r=4.2mm half-angle=45deg, axis (0,0,-1), area 2.5mm2, adj f54,f65,f122,f126
  f125: cone r=10.9mm half-angle=45deg, axis (0,0,1), area 6mm2, adj f39,f54,f123,f127
  f126: cone r=19.2mm half-angle=45deg, axis (0,0,-1), area 2.9mm2, adj f44,f54,f124,f128
  f127: cone r=4.2mm half-angle=45deg, axis (0,0,-1), area 2.5mm2, adj f54,f70,f125,f129
  f128: cone r=4.2mm half-angle=45deg, axis (0,0,-1), area 2.5mm2, adj f54,f64,f126,f130
  f129: cone r=19.2mm half-angle=45deg, axis (0,0,-1), area 2.9mm2, adj f38,f54,f127,f131
  f130: cone r=10.9mm half-angle=45deg, axis (0,0,1), area 6mm2, adj f45,f54,f128,f132
  f131: cone r=4.2mm half-angle=45deg, axis (0,0,-1), area 2.5mm2, adj f54,f71,f129,f133
  f132: cone r=4.2mm half-angle=45deg, axis (0,0,-1), area 2.5mm2, adj f54,f63,f130,f134
  f133: cone r=10.9mm half-angle=45deg, axis (0,0,1), area 6mm2, adj f37,f54,f131,f135
  f134: cone r=19.2mm half-angle=45deg, axis (0,0,-1), area 2.9mm2, adj f46,f54,f132,f136
  f135: cone r=4.2mm half-angle=45deg, axis (0,0,-1), area 2.5mm2, adj f54,f72,f133,f137
  f136: cone r=4.2mm half-angle=45deg, axis (0,0,-1), area 2.5mm2, adj f54,f62,f134,f138
  f137: cone r=19.2mm half-angle=45deg, axis (0,0,-1), area 2.9mm2, adj f36,f54,f135,f139
  f138: cone r=10.9mm half-angle=45deg, axis (0,0,1), area 6mm2, adj f47,f54,f136,f140
  f139: cone r=4.2mm half-angle=45deg, axis (0,0,-1), area 2.5mm2, adj f54,f73,f137,f141
  f140: cone r=4.2mm half-angle=45deg, axis (0,0,-1), area 2.5mm2, adj f54,f61,f138,f142
  f141: cone r=10.9mm half-angle=45deg, axis (0,0,1), area 6mm2, adj f35,f54,f139,f143
  f142: cone r=19.2mm half-angle=45deg, axis (0,0,-1), area 2.9mm2, adj f48,f54,f140,f144
  f143: cone r=4.2mm half-angle=45deg, axis (0,0,-1), area 2.5mm2, adj f54,f74,f141,f145
  f144: cone r=4.2mm half-angle=45deg, axis (0,0,-1), area 2.5mm2, adj f54,f60,f142,f146
  f145: cone r=19.2mm half-angle=45deg, axis (0,0,-1), area 2.9mm2, adj f34,f54,f143,f147
  f146: cone r=10.9mm half-angle=45deg, axis (0,0,1), area 6mm2, adj f49,f54,f144,f148
  f147: cone r=4.2mm half-angle=45deg, axis (0,0,-1), area 2.5mm2, adj f54,f75,f145,f149
  f148: cone r=4.2mm half-angle=45deg, axis (0,0,-1), area 2.5mm2, adj f54,f59,f146,f150
  f149: cone r=10.9mm half-angle=45deg, axis (0,0,1), area 6mm2, adj f53,f54,f147,f151
  f150: cone r=19.2mm half-angle=45deg, axis (0,0,-1), area 2.9mm2, adj f50,f54,f148,f152
  f151: cone r=4.2mm half-angle=45deg, axis (0,0,-1), area 2.5mm2, adj f54,f56,f149,f153
  f152: cone r=4.2mm half-angle=45deg, axis (0,0,-1), area 2.5mm2, adj f54,f58,f150,f154
  f153: cone r=19.2mm half-angle=45deg, axis (0,0,-1), area 2.9mm2, adj f52,f54,f151,f155
  f154: cone r=10.9mm half-angle=45deg, axis (0,0,1), area 6mm2, adj f51,f54,f152,f155
  f155: cone r=4.2mm half-angle=45deg, axis (0,0,-1), area 2.5mm2, adj f54,f57,f153,f154
PLACE A rot(axis=(0,1,0),180deg) t=(42.24,1.96,43.48)mm
PLACE B rot(axis=(0,-1,0),0deg) t=(-4.14,5.64,-6.52)mm
MATE fastened B.f12 <-> A.f13  axis (0,0,1) through (2.24,1.96,4.48)mm
